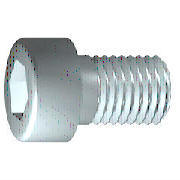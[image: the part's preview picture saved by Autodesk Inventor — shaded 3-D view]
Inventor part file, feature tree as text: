
AUTODESK INVENTOR PART (.ipt)
format: ipt  version: 2017 (Build 210142000, 142)  size: 182,784 bytes
history: native  units: mm (DEFAULTED — no unit token found)
features: sketch x2, extrude x1, plane x1, fillet x1
ambient origin geometry x7: Origin, YZ Plane, XY Plane, X Axis, Y Axis, Z Axis, Center Point
bodies: Solid1 (feature_tree), Body (feature_tree)
feature tree (5):
  extrude  "Slot"  Depth=5.0mm
  plane  "Work Plane1"
  fillet  "Fillet2"  Radius=5.0mm
  sketch  "Sketch1"  dims[d1=22.0mm d2=0.49086mm d3=5.0mm]
  sketch  "Sketch2"  dims[d4=2.5mm d5=60.0deg d6=5.0mm d7=5.0mm d8=4.618802mm d9=8.5mm d10=90.0deg d11=10.0mm d12=0.0mm d13=22.0mm d14=0.0mm d15=0.49076mm d16=0.49076mm d17=0.5mm d19=0.0mm d26=45.0mm d27=45.0deg d28=0.0mm d29=0.0mm d30=0.1mm]
